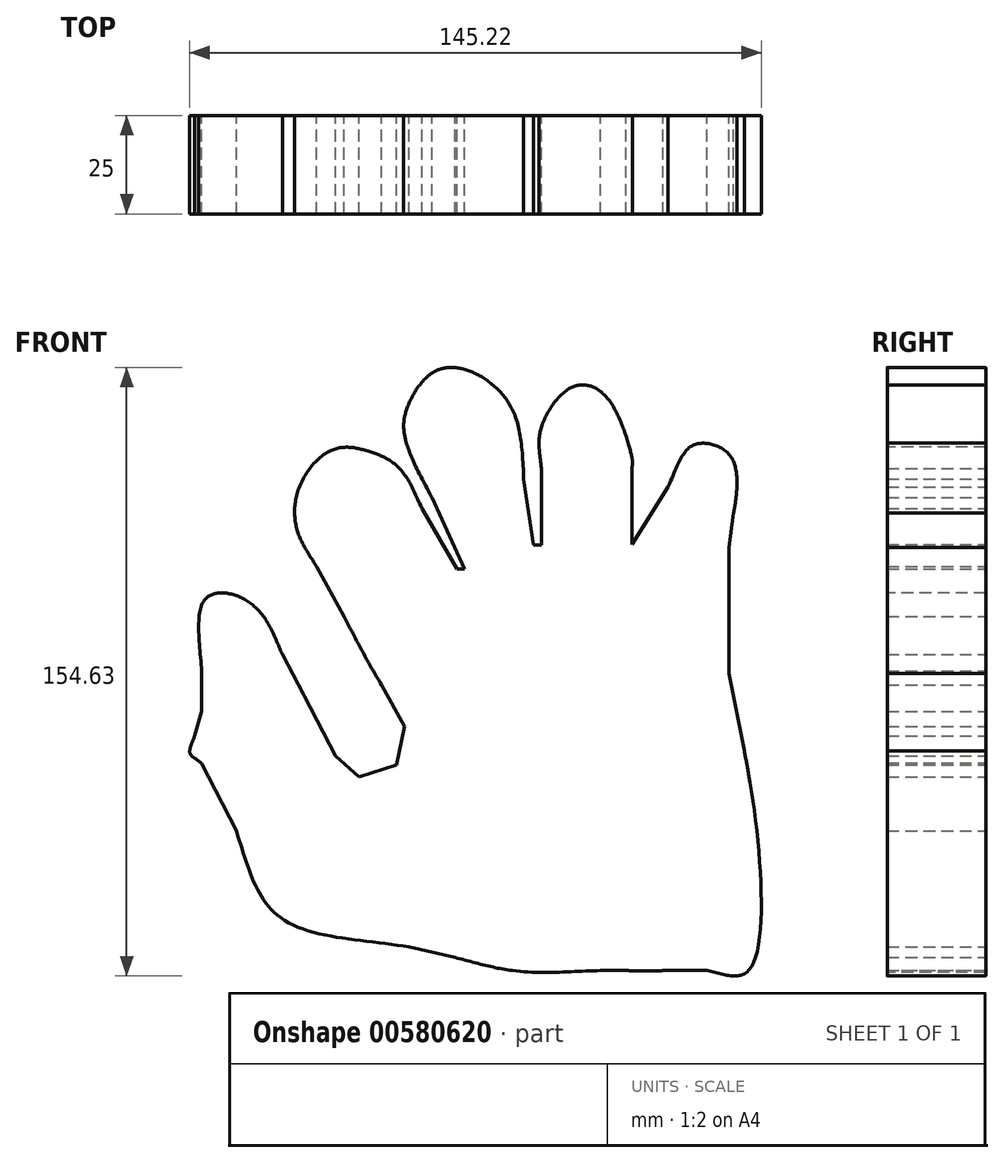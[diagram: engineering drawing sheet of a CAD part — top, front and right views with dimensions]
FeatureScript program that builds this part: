
annotation { "Feature Type Name" : "Feature", "Feature Type Description" : "" }
export const myFeature = defineFeature(function(context is Context, id is Id, definition is map)
    precondition{}
    {
        {
            var Q0;
            Q0=qCreatedBy(makeId("Front.planeOp"),FACE);
            var sketch = newSketch(context, id + "F0", { "sketchPlane" : qUnion([Q0])});
            skLineSegment(sketch, "E0", {"start": v(-6.6, -64.84) * mm, "end": v(53.4, -64.84) * mm});
            skLineSegment(sketch, "E1", {"start": v(53.4, -64.84) * mm, "end": v(53.4, -14.84) * mm});
            skLineSegment(sketch, "E2", {"start": v(53.4, -14.84) * mm, "end": v(48.4, 10.68) * mm});
            skLineSegment(sketch, "E3", {"start": v(48.4, 10.68) * mm, "end": v(48.4, 42.68) * mm});
            skLineSegment(sketch, "E4", {"start": v(48.4, 42.68) * mm, "end": v(50.4, 57.54) * mm});
            skLineSegment(sketch, "E5", {"start": v(50.4, 57.54) * mm, "end": v(48.4, 66.32) * mm});
            skLineSegment(sketch, "E6", {"start": v(48.4, 66.32) * mm, "end": v(39.76, 68.82) * mm});
            skLineSegment(sketch, "E7", {"start": v(39.76, 68.82) * mm, "end": v(23.76, 43.44) * mm});
            skLineSegment(sketch, "E8", {"start": v(23.76, 43.44) * mm, "end": v(23.76, 65.44) * mm});
            skLineSegment(sketch, "E9", {"start": v(23.76, 65.44) * mm, "end": v(20.76, 74.98) * mm});
            skLineSegment(sketch, "E10", {"start": v(20.76, 74.98) * mm, "end": v(14.76, 82.98) * mm});
            skLineSegment(sketch, "E11", {"start": v(14.76, 82.98) * mm, "end": v(7.76, 82.98) * mm});
            skLineSegment(sketch, "E12", {"start": v(7.76, 82.98) * mm, "end": v(0.76, 73.23) * mm});
            skLineSegment(sketch, "E13", {"start": v(0.76, 73.23) * mm, "end": v(0.76, 43.23) * mm});
            skLineSegment(sketch, "E14", {"start": v(0.76, 43.23) * mm, "end": v(-1.24, 43.23) * mm});
            skLineSegment(sketch, "E15", {"start": v(-1.24, 43.23) * mm, "end": v(-6.24, 76.86) * mm});
            skLineSegment(sketch, "E16", {"start": v(-6.24, 76.86) * mm, "end": v(-13.74, 85.58) * mm});
            skLineSegment(sketch, "E17", {"start": v(-28.74, 85.58) * mm, "end": v(-33.74, 76.92) * mm});
            skLineSegment(sketch, "E18", {"start": v(-33.74, 76.92) * mm, "end": v(-33.74, 69.92) * mm});
            skLineSegment(sketch, "E19", {"start": v(-33.74, 69.92) * mm, "end": v(-18.74, 37.2) * mm});
            skLineSegment(sketch, "E20", {"start": v(-18.74, 37.2) * mm, "end": v(-20.74, 37.2) * mm});
            skLineSegment(sketch, "E21", {"start": v(-20.74, 37.2) * mm, "end": v(-35.74, 63.17) * mm});
            skLineSegment(sketch, "E22", {"start": v(-35.74, 63.17) * mm, "end": v(-43.74, 67.3) * mm});
            skLineSegment(sketch, "E23", {"start": v(-43.74, 67.3) * mm, "end": v(-52.74, 67.3) * mm});
            skLineSegment(sketch, "E24", {"start": v(-52.74, 67.3) * mm, "end": v(-61.02, 57.28) * mm});
            skLineSegment(sketch, "E25", {"start": v(-61.02, 57.28) * mm, "end": v(-61.02, 46.28) * mm});
            skLineSegment(sketch, "E26", {"start": v(-61.02, 46.28) * mm, "end": v(-34.02, -2.78) * mm});
            skLineSegment(sketch, "E27", {"start": v(-34.02, -2.78) * mm, "end": v(-36.02, -12.58) * mm});
            skLineSegment(sketch, "E28", {"start": v(-36.02, -12.58) * mm, "end": v(-45.56, -15.58) * mm});
            skLineSegment(sketch, "E29", {"start": v(-45.56, -15.58) * mm, "end": v(-51.56, -10.29) * mm});
            skLineSegment(sketch, "E30", {"start": v(-51.56, -10.29) * mm, "end": v(-70.56, 26.04) * mm});
            skLineSegment(sketch, "E31", {"start": v(-70.56, 26.04) * mm, "end": v(-79.22, 31.04) * mm});
            skLineSegment(sketch, "E32", {"start": v(-79.22, 31.04) * mm, "end": v(-79.22, 28.04) * mm});
            skLineSegment(sketch, "E33", {"start": v(-79.22, 31.04) * mm, "end": v(-85.55, 28.04) * mm});
            skLineSegment(sketch, "E34", {"start": v(-85.55, 28.04) * mm, "end": v(-85.55, 1.04) * mm});
            skLineSegment(sketch, "E35", {"start": v(-85.55, 1.04) * mm, "end": v(-88.55, -9.54) * mm});
            skLineSegment(sketch, "E36", {"start": v(-88.55, -9.54) * mm, "end": v(-85.55, -12.19) * mm});
            skLineSegment(sketch, "E37", {"start": v(-85.55, -12.19) * mm, "end": v(-65.55, -51.38) * mm});
            skLineSegment(sketch, "E38", {"start": v(-65.55, -51.38) * mm, "end": v(-6.6, -64.84) * mm});
            skLineSegment(sketch, "E39", {"start": v(-65.55, -51.38) * mm, "end": v(-44.93, -34.8) * mm});
            skLineSegment(sketch, "E40", {"start": v(-44.93, -34.8) * mm, "end": v(-5.2, -48.3) * mm});
            skLineSegment(sketch, "E41", {"start": v(-5.2, -48.3) * mm, "end": v(-6.6, -64.84) * mm});
            skLineSegment(sketch, "E42", {"start": v(-5.2, -48.3) * mm, "end": v(15.79, -48.3) * mm});
            skLineSegment(sketch, "E43", {"start": v(15.79, -48.3) * mm, "end": v(15.79, -64.84) * mm});
            skLineSegment(sketch, "E44", {"start": v(15.79, -64.84) * mm, "end": v(15.79, -48.3) * mm});
            skLineSegment(sketch, "E45", {"start": v(15.79, -48.3) * mm, "end": v(31.68, -48.3) * mm});
            skLineSegment(sketch, "E46", {"start": v(31.68, -48.3) * mm, "end": v(31.68, -64.84) * mm});
            skLineSegment(sketch, "E47", {"start": v(31.68, -64.84) * mm, "end": v(31.68, -48.3) * mm});
            skLineSegment(sketch, "E48", {"start": v(31.68, -48.3) * mm, "end": v(42.8, -48.3) * mm});
            skLineSegment(sketch, "E49", {"start": v(42.8, -48.3) * mm, "end": v(42.8, -64.84) * mm});
            skLineSegment(sketch, "E50", {"start": v(42.8, -64.84) * mm, "end": v(42.8, -48.3) * mm});
            skLineSegment(sketch, "E51", {"start": v(42.8, -48.3) * mm, "end": v(37.56, -15.08) * mm});
            skLineSegment(sketch, "E52", {"start": v(37.56, -15.08) * mm, "end": v(53.4, -14.84) * mm});
            skLineSegment(sketch, "E53", {"start": v(31.68, -48.3) * mm, "end": v(24.85, -15.88) * mm});
            skLineSegment(sketch, "E54", {"start": v(24.85, -15.88) * mm, "end": v(37.56, -15.08) * mm});
            skLineSegment(sketch, "E55", {"start": v(15.79, -48.3) * mm, "end": v(10.07, -16.51) * mm});
            skLineSegment(sketch, "E56", {"start": v(10.07, -16.51) * mm, "end": v(24.85, -15.88) * mm});
            skLineSegment(sketch, "E57", {"start": v(-5.2, -48.3) * mm, "end": v(-8.7, -16.04) * mm});
            skLineSegment(sketch, "E58", {"start": v(-8.7, -16.04) * mm, "end": v(10.07, -16.51) * mm});
            skLineSegment(sketch, "E59", {"start": v(-36.02, -12.58) * mm, "end": v(-8.7, -16.04) * mm});
            skLineSegment(sketch, "E60", {"start": v(-45.56, -15.58) * mm, "end": v(-44.93, -34.8) * mm});
            skLineSegment(sketch, "E61", {"start": v(-26.95, -40.9) * mm, "end": v(-22.36, -14.3) * mm});
            skLineSegment(sketch, "E62", {"start": v(-22.36, -14.3) * mm, "end": v(-26.95, -40.9) * mm});
            skLineSegment(sketch, "E63", {"start": v(-26.95, -40.9) * mm, "end": v(-32.9, -58.83) * mm});
            skLineSegment(sketch, "E64", {"start": v(-32.9, -58.83) * mm, "end": v(-26.95, -40.9) * mm});
            skLineSegment(sketch, "E65", {"start": v(-76.76, -29.41) * mm, "end": v(-62.41, -20.17) * mm});
            skLineSegment(sketch, "E66", {"start": v(-62.41, -20.17) * mm, "end": v(-44.93, -34.8) * mm});
            skLineSegment(sketch, "E67", {"start": v(-62.41, -20.17) * mm, "end": v(-71, -3.64) * mm});
            skLineSegment(sketch, "E68", {"start": v(-71, -3.64) * mm, "end": v(-51.56, -10.29) * mm});
            skLineSegment(sketch, "E69", {"start": v(-62.41, -20.17) * mm, "end": v(-51.56, -10.29) * mm});
            skLineSegment(sketch, "E70", {"start": v(-85.55, -12.19) * mm, "end": v(-71, -3.64) * mm});
            skLineSegment(sketch, "E71", {"start": v(-71, -3.64) * mm, "end": v(-59.48, 4.84) * mm});
            skLineSegment(sketch, "E72", {"start": v(-59.48, 4.84) * mm, "end": v(-71, -3.64) * mm});
            skLineSegment(sketch, "E73", {"start": v(-71, -3.64) * mm, "end": v(-78.11, 8.47) * mm});
            skLineSegment(sketch, "E74", {"start": v(-78.11, 8.47) * mm, "end": v(-70.56, 26.04) * mm});
            skLineSegment(sketch, "E75", {"start": v(-78.11, 8.47) * mm, "end": v(-85.55, 1.04) * mm});
            skLineSegment(sketch, "E76", {"start": v(-78.11, 8.47) * mm, "end": v(-80.53, 22.59) * mm});
            skLineSegment(sketch, "E77", {"start": v(-80.53, 22.59) * mm, "end": v(-79.22, 31.04) * mm});
            skLineSegment(sketch, "E78", {"start": v(-80.53, 22.59) * mm, "end": v(-85.55, 28.04) * mm});
            skLineSegment(sketch, "E79", {"start": v(-88.55, -9.54) * mm, "end": v(-79.42, -2.2) * mm});
            skLineSegment(sketch, "E80", {"start": v(-79.42, -2.2) * mm, "end": v(-74.55, 2.42) * mm});
            skLineSegment(sketch, "E81", {"start": v(-74.55, 2.42) * mm, "end": v(-65.04, 15.48) * mm});
            skLineSegment(sketch, "E82", {"start": v(-65.04, 15.48) * mm, "end": v(-74.55, 2.42) * mm});
            skLineSegment(sketch, "E83", {"start": v(-22.36, -14.3) * mm, "end": v(-20.74, 37.2) * mm});
            skLineSegment(sketch, "E84", {"start": v(-8.7, -16.04) * mm, "end": v(-18.74, 37.2) * mm});
            skLineSegment(sketch, "E85", {"start": v(10.07, -16.51) * mm, "end": v(-1.24, 43.23) * mm});
            skLineSegment(sketch, "E86", {"start": v(24.85, -15.88) * mm, "end": v(0.76, 43.23) * mm});
            skLineSegment(sketch, "E87", {"start": v(37.56, -15.08) * mm, "end": v(23.76, 43.44) * mm});
            skLineSegment(sketch, "E88", {"start": v(48.4, 10.68) * mm, "end": v(31.49, 10.68) * mm});
            skLineSegment(sketch, "E89", {"start": v(31.49, 10.68) * mm, "end": v(14.03, 10.68) * mm});
            skLineSegment(sketch, "E90", {"start": v(14.03, 10.68) * mm, "end": v(4.92, 10.68) * mm});
            skLineSegment(sketch, "E91", {"start": v(4.92, 10.68) * mm, "end": v(-13.5, 9.39) * mm});
            skLineSegment(sketch, "E92", {"start": v(-13.5, 9.39) * mm, "end": v(-21.61, 9.39) * mm});
            skLineSegment(sketch, "E93", {"start": v(-21.61, 9.39) * mm, "end": v(-39.82, 7.75) * mm});
            skLineSegment(sketch, "E94", {"start": v(-39.82, 7.75) * mm, "end": v(-49.4, 25.15) * mm});
            skLineSegment(sketch, "E95", {"start": v(-49.4, 25.15) * mm, "end": v(-20.74, 37.2) * mm});
            skLineSegment(sketch, "E96", {"start": v(-18.74, 37.2) * mm, "end": v(0, 37.2) * mm});
            skLineSegment(sketch, "E97", {"start": v(0, 37.2) * mm, "end": v(2.76, 38.32) * mm});
            skLineSegment(sketch, "E98", {"start": v(2.76, 38.32) * mm, "end": v(24.97, 38.32) * mm});
            skLineSegment(sketch, "E99", {"start": v(24.97, 38.32) * mm, "end": v(48.4, 36.1) * mm});
            skLineSegment(sketch, "E100", {"start": v(-56.38, 37.83) * mm, "end": v(-29.61, 52.56) * mm});
            skLineSegment(sketch, "E101", {"start": v(-29.61, 52.56) * mm, "end": v(-56.38, 37.83) * mm});
            skLineSegment(sketch, "E102", {"start": v(-27.06, 55.35) * mm, "end": v(-4.05, 62.15) * mm});
            skLineSegment(sketch, "E103", {"start": v(-4.05, 62.15) * mm, "end": v(-27.06, 55.35) * mm});
            skLineSegment(sketch, "E104", {"start": v(0.76, 62.73) * mm, "end": v(23.76, 62.73) * mm});
            skLineSegment(sketch, "E105", {"start": v(23.76, 62.73) * mm, "end": v(0.76, 62.73) * mm});
            skLineSegment(sketch, "E106", {"start": v(32.95, 58.02) * mm, "end": v(49.58, 51.37) * mm});
            skLineSegment(sketch, "E107", {"start": v(49.58, 51.37) * mm, "end": v(32.95, 58.02) * mm});
            skLineSegment(sketch, "E108", {"start": v(-9.37, 37.2) * mm, "end": v(-15.56, 58.75) * mm});
            skLineSegment(sketch, "E109", {"start": v(-15.56, 58.75) * mm, "end": v(-22.46, 88.4) * mm});
            skLineSegment(sketch, "E110", {"start": v(-22.46, 88.4) * mm, "end": v(-19.37, 75.14) * mm});
            skLineSegment(sketch, "E111", {"start": v(-19.37, 75.14) * mm, "end": v(-33.74, 69.92) * mm});
            skLineSegment(sketch, "E112", {"start": v(-19.37, 75.14) * mm, "end": v(-6.24, 76.86) * mm});
            skLineSegment(sketch, "E113", {"start": v(0.76, 73.23) * mm, "end": v(11.33, 73.23) * mm});
            skLineSegment(sketch, "E114", {"start": v(11.33, 73.23) * mm, "end": v(20.76, 74.98) * mm});
            skLineSegment(sketch, "E115", {"start": v(-43, 45.2) * mm, "end": v(-54.2, 65.54) * mm});
            skLineSegment(sketch, "E116", {"start": v(-54.2, 65.54) * mm, "end": v(-48.6, 55.37) * mm});
            skLineSegment(sketch, "E117", {"start": v(-48.6, 55.37) * mm, "end": v(-35.74, 63.17) * mm});
            skLineSegment(sketch, "E118", {"start": v(-61.02, 46.28) * mm, "end": v(-48.6, 55.37) * mm});
            skFitSpline(sketch, "E119", {"points": [v(-85.55, 28.04) * mm, v(-79.22, 31.04) * mm, v(-70.56, 26.04) * mm, v(-65.04, 15.48) * mm, v(-59.48, 4.84) * mm, v(-51.56, -10.29) * mm, v(-45.56, -15.58) * mm, v(-36.02, -12.58) * mm, v(-34.02, -2.78) * mm, v(-39.82, 7.75) * mm, v(-49.4, 25.15) * mm, v(-56.38, 37.83) * mm, v(-61.02, 46.28) * mm, v(-61.02, 57.28) * mm, v(-52.74, 67.3) * mm, v(-43.74, 67.3) * mm, v(-35.74, 63.17) * mm, v(-29.61, 52.56) * mm, v(-20.74, 37.2) * mm, v(-18.74, 37.2) * mm, v(-27.06, 55.35) * mm, v(-33.74, 69.92) * mm, v(-33.74, 76.92) * mm, v(-28.74, 85.58) * mm, v(-22.46, 88.4) * mm, v(-13.74, 85.58) * mm, v(-6.24, 76.86) * mm, v(-3.74, 60.05) * mm, v(-1.24, 43.23) * mm, v(0.76, 43.23) * mm, v(0.76, 62.73) * mm, v(0.76, 73.23) * mm, v(7.76, 82.98) * mm, v(14.76, 82.98) * mm, v(20.76, 74.98) * mm, v(23.76, 65.44) * mm, v(23.76, 62.73) * mm, v(23.76, 43.44) * mm, v(32.95, 58.02) * mm, v(39.76, 68.82) * mm, v(48.4, 66.32) * mm, v(50.4, 57.54) * mm, v(49.58, 51.37) * mm, v(48.4, 42.68) * mm, v(48.4, 36.1) * mm, v(48.4, 10.68) * mm, v(53.4, -14.84) * mm, v(53.4, -64.84) * mm, v(42.8, -64.84) * mm, v(31.68, -64.84) * mm, v(15.79, -64.84) * mm, v(-6.6, -64.84) * mm, v(-32.9, -58.83) * mm, v(-65.55, -51.38) * mm, v(-76.76, -29.41) * mm, v(-85.55, -12.19) * mm, v(-88.55, -9.54) * mm, v(-85.55, 1.04) * mm, v(-85.55, 28.04) * mm]});
            skSolve(sketch);
        }
        {
            var Q0;
            Q0=qSketchRegion(id+"F0",true);
            var Q1;
            {var subQ0=sQuery(id+"F0.wireOp",EDGE,"E57");Q1=makeQuery(id+"F0.imprint","IMPRINT",FACE,{"disambiguationData":[TD([[makeQuery(id+"F0.imprint","IMPRINT",EDGE,{"derivedFrom":subQ0}),1.0]])]});}
            var Q2;
            {var subQ5=sQuery(id+"F0.wireOp",EDGE,"E92");Q2=makeQuery(id+"F0.imprint","IMPRINT",FACE,{"disambiguationData":[TD([[makeQuery(id+"F0.imprint","IMPRINT",EDGE,{"derivedFrom":subQ5}),1.0]])]});}
            var Q3;
            {var subQ0=sQuery(id+"F0.wireOp",EDGE,"E58");Q3=makeQuery(id+"F0.imprint","IMPRINT",FACE,{"disambiguationData":[TD([[makeQuery(id+"F0.imprint","IMPRINT",EDGE,{"derivedFrom":subQ0}),1.0]])]});}
            var Q4;
            Q4=makeQuery(id+"F0.imprint","IMPRINT",FACE,{"disambiguationData":[TD([[makeQuery(id+"F0.imprint","IMPRINT",EDGE,{"derivedFrom":sQuery(id+"F0.wireOp",EDGE,"E42")}),1.0]])]});
            var Q5;
            Q5=makeQuery(id+"F0.imprint","IMPRINT",FACE,{"disambiguationData":[TD([[makeQuery(id+"F0.imprint","IMPRINT",EDGE,{"derivedFrom":sQuery(id+"F0.wireOp",EDGE,"E45")}),1.0]])]});
            var Q6;
            Q6=makeQuery(id+"F0.imprint","IMPRINT",FACE,{"disambiguationData":[TD([[makeQuery(id+"F0.imprint","IMPRINT",EDGE,{"derivedFrom":sQuery(id+"F0.wireOp",EDGE,"E48")}),1.0]])]});
            var Q7;
            {var subQ0=sQuery(id+"F0.wireOp",EDGE,"E54");Q7=makeQuery(id+"F0.imprint","IMPRINT",FACE,{"disambiguationData":[TD([[makeQuery(id+"F0.imprint","IMPRINT",EDGE,{"derivedFrom":subQ0}),1.0]])]});}
            var Q8;
            {var subQ0=sQuery(id+"F0.wireOp",EDGE,"E56");Q8=makeQuery(id+"F0.imprint","IMPRINT",FACE,{"disambiguationData":[TD([[makeQuery(id+"F0.imprint","IMPRINT",EDGE,{"derivedFrom":subQ0}),1.0]])]});}
            var Q9;
            {var subQ0=sQuery(id+"F0.wireOp",EDGE,"E90");Q9=makeQuery(id+"F0.imprint","IMPRINT",FACE,{"disambiguationData":[TD([[makeQuery(id+"F0.imprint","IMPRINT",EDGE,{"derivedFrom":subQ0}),-1.0]])]});}
            var Q10;
            {var subQ0=sQuery(id+"F0.wireOp",EDGE,"E89");Q10=makeQuery(id+"F0.imprint","IMPRINT",FACE,{"disambiguationData":[TD([[makeQuery(id+"F0.imprint","IMPRINT",EDGE,{"derivedFrom":subQ0}),-1.0]])]});}
            var Q11;
            Q11=makeQuery(id+"F0.imprint","IMPRINT",FACE,{"disambiguationData":[TD([[makeQuery(id+"F0.imprint","IMPRINT",EDGE,{"derivedFrom":sQuery(id+"F0.wireOp",EDGE,"E10")}),1.0]])]});
            extrude(context, id + "F1", {"entities" : qUnion([Q0, Q1, Q2, Q3, Q4, Q5, Q6, Q7, Q8, Q9, Q10, Q11]), "endBound" : BoundingType.SYMMETRIC, "depth" : 25 * mm});
        }
    });
